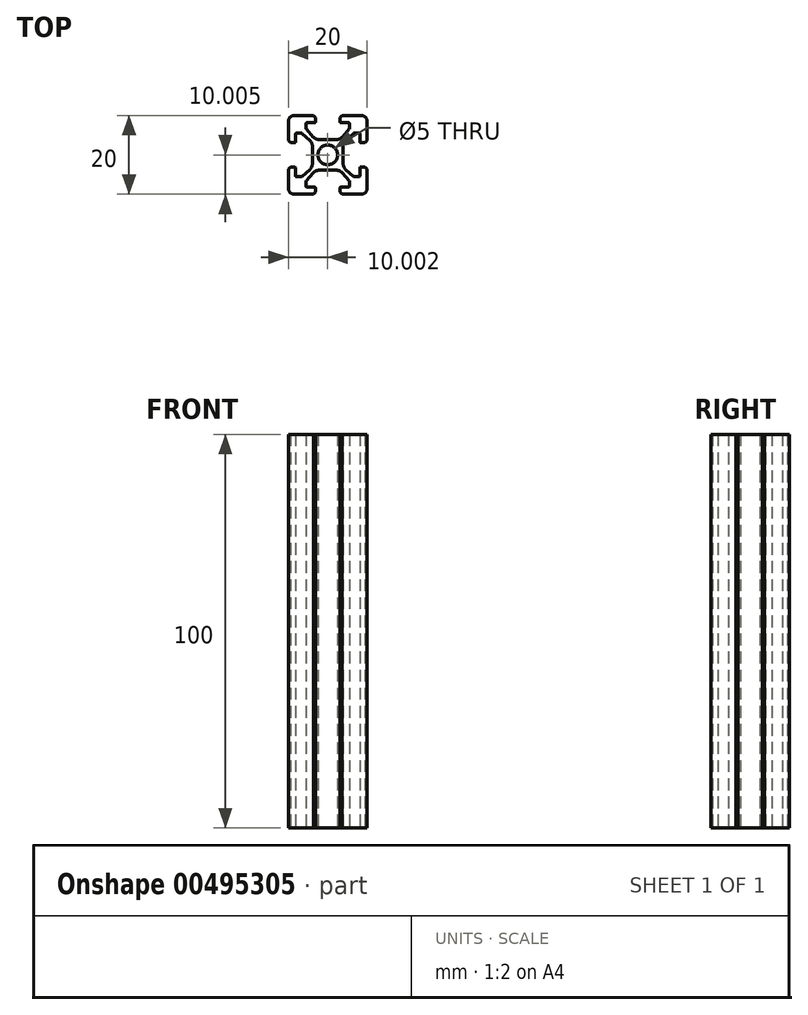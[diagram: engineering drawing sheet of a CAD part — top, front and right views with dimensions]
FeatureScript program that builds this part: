
annotation { "Feature Type Name" : "Feature", "Feature Type Description" : "" }
export const myFeature = defineFeature(function(context is Context, id is Id, definition is map)
    precondition{}
    {
        {
            var Q0;
            Q0=qCreatedBy(makeId("Top.planeOp"),FACE);
            var sketch = newSketch(context, id + "F0", { "sketchPlane" : qUnion([Q0])});
            skLineSegment(sketch, "E0", {"start": v(30.58, 14.76) * mm, "end": v(30.58, 13.66) * mm});
            skLineSegment(sketch, "E1", {"start": v(30.38, 13.46) * mm, "end": v(28.38, 13.46) * mm});
            skLineSegment(sketch, "E2", {"start": v(28.18, 13.26) * mm, "end": v(28.18, 11.94) * mm});
            skLineSegment(sketch, "E3", {"start": v(28.23, 11.8) * mm, "end": v(29.99, 9.84) * mm});
            skLineSegment(sketch, "E4", {"start": v(31.48, 9.16) * mm, "end": v(33.68, 9.16) * mm});
            skPoint(sketch, "E5.visualSharp", {"position": v(23.68, 15.26) * mm});
            skArc(sketch, "E5.filletArc", {"start": v(25.18, 15.26) * mm, "mid": v(24.6, 15.15) * mm, "end": v(24.1, 14.81) * mm});
            skPoint(sketch, "E6.visualSharp", {"position": v(30.58, 9.16) * mm});
            skArc(sketch, "E6.filletArc", {"start": v(29.99, 9.84) * mm, "mid": v(30.66, 9.34) * mm, "end": v(31.48, 9.16) * mm});
            skLineSegment(sketch, "E7", {"start": v(25.18, 15.26) * mm, "end": v(30.08, 15.26) * mm});
            skPoint(sketch, "E8.visualSharp", {"position": v(30.08, 14.76) * mm});
            skPoint(sketch, "E9.visualSharp", {"position": v(30.58, 13.46) * mm});
            skArc(sketch, "E9.filletArc", {"start": v(30.38, 13.46) * mm, "mid": v(30.52, 13.52) * mm, "end": v(30.58, 13.66) * mm});
            skPoint(sketch, "E10.visualSharp", {"position": v(28.18, 13.46) * mm});
            skArc(sketch, "E10.filletArc", {"start": v(28.38, 13.46) * mm, "mid": v(28.24, 13.4) * mm, "end": v(28.18, 13.26) * mm});
            skPoint(sketch, "E11.visualSharp", {"position": v(28.18, 11.86) * mm});
            skArc(sketch, "E11.filletArc", {"start": v(28.18, 11.94) * mm, "mid": v(28.2, 11.87) * mm, "end": v(28.23, 11.8) * mm});
            skLineSegment(sketch, "E12", {"start": v(30.08, 15.26) * mm, "end": v(30.58, 14.76) * mm});
            skLineSegment(sketch, "E13", {"start": v(24.12, 14.83) * mm, "end": v(24.12, 14.83) * mm});
            skArc(sketch, "E14.MirrorCS", {"start": v(25.48, 8.56) * mm, "mid": v(25.42, 8.42) * mm, "end": v(25.28, 8.36) * mm});
            skArc(sketch, "E15.MirrorCS", {"start": v(27, 10.76) * mm, "mid": v(27.08, 10.75) * mm, "end": v(27.14, 10.71) * mm});
            skArc(sketch, "E16.MirrorCS", {"start": v(25.48, 10.56) * mm, "mid": v(25.54, 10.7) * mm, "end": v(25.68, 10.76) * mm});
            skPoint(sketch, "E17.MirrorP", {"position": v(27.08, 10.76) * mm});
            skLineSegment(sketch, "E18.MirrorCS", {"start": v(23.68, 8.86) * mm, "end": v(24.18, 8.36) * mm});
            skLineSegment(sketch, "E19.MirrorCS", {"start": v(23.68, 13.76) * mm, "end": v(23.68, 8.86) * mm});
            skLineSegment(sketch, "E20.MirrorCS", {"start": v(25.68, 10.76) * mm, "end": v(27, 10.76) * mm});
            skLineSegment(sketch, "E21.MirrorCS", {"start": v(29.78, 7.47) * mm, "end": v(29.78, 5.26) * mm});
            skLineSegment(sketch, "E22.MirrorCS", {"start": v(27.14, 10.71) * mm, "end": v(29.11, 8.96) * mm});
            skLineSegment(sketch, "E23.MirrorCS", {"start": v(25.48, 8.56) * mm, "end": v(25.48, 10.56) * mm});
            skArc(sketch, "E24.MirrorCS", {"start": v(23.68, 13.76) * mm, "mid": v(23.8, 14.35) * mm, "end": v(24.13, 14.84) * mm});
            skPoint(sketch, "E25.MirrorP", {"position": v(29.78, 8.36) * mm});
            skPoint(sketch, "E26.MirrorP", {"position": v(25.48, 10.76) * mm});
            skPoint(sketch, "E27.MirrorP", {"position": v(24.18, 8.86) * mm});
            skPoint(sketch, "E28.MirrorP", {"position": v(25.48, 8.36) * mm});
            skLineSegment(sketch, "E29.MirrorCS", {"start": v(24.18, 8.36) * mm, "end": v(25.28, 8.36) * mm});
            skArc(sketch, "E30.MirrorCS", {"start": v(29.11, 8.96) * mm, "mid": v(29.6, 8.29) * mm, "end": v(29.78, 7.47) * mm});
            skArc(sketch, "E31.MirrorCS", {"start": v(39.18, 11.94) * mm, "mid": v(39.17, 11.87) * mm, "end": v(39.13, 11.8) * mm});
            skArc(sketch, "E32.MirrorCS", {"start": v(40.36, 10.76) * mm, "mid": v(40.29, 10.75) * mm, "end": v(40.23, 10.71) * mm});
            skArc(sketch, "E33.MirrorCS", {"start": v(41.88, 8.56) * mm, "mid": v(41.94, 8.42) * mm, "end": v(42.08, 8.36) * mm});
            skArc(sketch, "E34.MirrorCS", {"start": v(38.98, 13.46) * mm, "mid": v(39.12, 13.4) * mm, "end": v(39.18, 13.26) * mm});
            skArc(sketch, "E35.MirrorCS", {"start": v(36.98, 13.46) * mm, "mid": v(36.84, 13.52) * mm, "end": v(36.78, 13.66) * mm});
            skArc(sketch, "E36.MirrorCS", {"start": v(41.88, 10.56) * mm, "mid": v(41.82, 10.7) * mm, "end": v(41.68, 10.76) * mm});
            skArc(sketch, "E37.MirrorCS", {"start": v(42.18, 15.26) * mm, "mid": v(42.76, 15.15) * mm, "end": v(43.26, 14.81) * mm});
            skLineSegment(sketch, "E38.MirrorCS", {"start": v(37.28, 15.26) * mm, "end": v(36.78, 14.76) * mm});
            skArc(sketch, "E39.MirrorCS", {"start": v(43.68, 13.76) * mm, "mid": v(43.56, 14.35) * mm, "end": v(43.23, 14.84) * mm});
            skLineSegment(sketch, "E40.MirrorCS", {"start": v(43.18, 8.36) * mm, "end": v(42.08, 8.36) * mm});
            skLineSegment(sketch, "E41.MirrorCS", {"start": v(36.78, 14.76) * mm, "end": v(36.78, 13.66) * mm});
            skLineSegment(sketch, "E42.MirrorCS", {"start": v(43.68, 8.86) * mm, "end": v(43.18, 8.36) * mm});
            skLineSegment(sketch, "E43.MirrorCS", {"start": v(39.18, 13.26) * mm, "end": v(39.18, 11.94) * mm});
            skArc(sketch, "E44.MirrorCS", {"start": v(38.25, 8.96) * mm, "mid": v(37.76, 8.29) * mm, "end": v(37.58, 7.47) * mm});
            skLineSegment(sketch, "E45.MirrorCS", {"start": v(36.98, 13.46) * mm, "end": v(38.98, 13.46) * mm});
            skArc(sketch, "E46.MirrorCS", {"start": v(37.38, 9.84) * mm, "mid": v(36.7, 9.34) * mm, "end": v(35.88, 9.16) * mm});
            skLineSegment(sketch, "E47.MirrorCS", {"start": v(43.24, 14.83) * mm, "end": v(43.24, 14.83) * mm});
            skPoint(sketch, "E48.MirrorP", {"position": v(43.18, 8.86) * mm});
            skLineSegment(sketch, "E49.MirrorCS", {"start": v(39.13, 11.8) * mm, "end": v(37.38, 9.84) * mm});
            skLineSegment(sketch, "E50.MirrorCS", {"start": v(41.88, 8.56) * mm, "end": v(41.88, 10.56) * mm});
            skPoint(sketch, "E51.MirrorP", {"position": v(41.88, 8.36) * mm});
            skLineSegment(sketch, "E52.MirrorCS", {"start": v(43.68, 13.76) * mm, "end": v(43.68, 8.86) * mm});
            skLineSegment(sketch, "E53.MirrorCS", {"start": v(42.18, 15.26) * mm, "end": v(37.28, 15.26) * mm});
            skPoint(sketch, "E54.MirrorP", {"position": v(41.88, 10.76) * mm});
            skPoint(sketch, "E55.MirrorP", {"position": v(36.78, 13.46) * mm});
            skLineSegment(sketch, "E56.MirrorCS", {"start": v(35.88, 9.16) * mm, "end": v(33.68, 9.16) * mm});
            skPoint(sketch, "E57.MirrorP", {"position": v(37.58, 8.36) * mm});
            skLineSegment(sketch, "E58.MirrorCS", {"start": v(37.58, 7.47) * mm, "end": v(37.58, 5.26) * mm});
            skPoint(sketch, "E59.MirrorP", {"position": v(37.28, 14.76) * mm});
            skLineSegment(sketch, "E60.MirrorCS", {"start": v(41.68, 10.76) * mm, "end": v(40.36, 10.76) * mm});
            skLineSegment(sketch, "E61.MirrorCS", {"start": v(40.23, 10.71) * mm, "end": v(38.25, 8.96) * mm});
            skPoint(sketch, "E62.MirrorP", {"position": v(43.68, 15.26) * mm});
            skPoint(sketch, "E63.MirrorP", {"position": v(36.78, 9.16) * mm});
            skPoint(sketch, "E64.MirrorP", {"position": v(39.18, 11.86) * mm});
            skPoint(sketch, "E65.MirrorP", {"position": v(40.28, 10.76) * mm});
            skPoint(sketch, "E66.MirrorP", {"position": v(39.18, 13.46) * mm});
            skArc(sketch, "E67.MirrorCS", {"start": v(40.36, -0.24) * mm, "mid": v(40.29, -0.22) * mm, "end": v(40.23, -0.18) * mm});
            skArc(sketch, "E68.MirrorCS", {"start": v(28.18, -1.41) * mm, "mid": v(28.2, -1.34) * mm, "end": v(28.23, -1.28) * mm});
            skLineSegment(sketch, "E69.MirrorCS", {"start": v(41.68, -0.24) * mm, "end": v(40.36, -0.24) * mm});
            skArc(sketch, "E70.MirrorCS", {"start": v(27, -0.24) * mm, "mid": v(27.08, -0.22) * mm, "end": v(27.14, -0.18) * mm});
            skArc(sketch, "E71.MirrorCS", {"start": v(41.88, -0.04) * mm, "mid": v(41.82, -0.18) * mm, "end": v(41.68, -0.24) * mm});
            skArc(sketch, "E72.MirrorCS", {"start": v(28.38, -2.94) * mm, "mid": v(28.24, -2.88) * mm, "end": v(28.18, -2.74) * mm});
            skLineSegment(sketch, "E73.MirrorCS", {"start": v(28.18, -2.74) * mm, "end": v(28.18, -1.41) * mm});
            skLineSegment(sketch, "E74.MirrorCS", {"start": v(25.68, -0.24) * mm, "end": v(27, -0.24) * mm});
            skArc(sketch, "E75.MirrorCS", {"start": v(25.48, -0.04) * mm, "mid": v(25.54, -0.18) * mm, "end": v(25.68, -0.24) * mm});
            skArc(sketch, "E76.MirrorCS", {"start": v(38.98, -2.94) * mm, "mid": v(39.12, -2.88) * mm, "end": v(39.18, -2.74) * mm});
            skLineSegment(sketch, "E77.MirrorCS", {"start": v(30.58, -4.24) * mm, "end": v(30.58, -3.14) * mm});
            skArc(sketch, "E78.MirrorCS", {"start": v(41.88, 1.96) * mm, "mid": v(41.94, 2.1) * mm, "end": v(42.08, 2.16) * mm});
            skArc(sketch, "E79.MirrorCS", {"start": v(39.18, -1.41) * mm, "mid": v(39.17, -1.34) * mm, "end": v(39.13, -1.28) * mm});
            skLineSegment(sketch, "E80.MirrorCS", {"start": v(39.18, -2.74) * mm, "end": v(39.18, -1.41) * mm});
            skArc(sketch, "E81.MirrorCS", {"start": v(36.98, -2.94) * mm, "mid": v(36.84, -3) * mm, "end": v(36.78, -3.14) * mm});
            skLineSegment(sketch, "E82.MirrorCS", {"start": v(30.08, -4.74) * mm, "end": v(30.58, -4.24) * mm});
            skArc(sketch, "E83.MirrorCS", {"start": v(30.38, -2.94) * mm, "mid": v(30.52, -3) * mm, "end": v(30.58, -3.14) * mm});
            skArc(sketch, "E84.MirrorCS", {"start": v(25.48, 1.96) * mm, "mid": v(25.42, 2.1) * mm, "end": v(25.28, 2.16) * mm});
            skLineSegment(sketch, "E85.MirrorCS", {"start": v(23.68, 1.66) * mm, "end": v(24.18, 2.16) * mm});
            skArc(sketch, "E86.MirrorCS", {"start": v(23.68, -3.24) * mm, "mid": v(23.8, -3.82) * mm, "end": v(24.13, -4.3) * mm});
            skLineSegment(sketch, "E87.MirrorCS", {"start": v(37.28, -4.74) * mm, "end": v(36.78, -4.24) * mm});
            skArc(sketch, "E88.MirrorCS", {"start": v(43.68, -3.24) * mm, "mid": v(43.56, -3.82) * mm, "end": v(43.23, -4.3) * mm});
            skArc(sketch, "E89.MirrorCS", {"start": v(29.99, 0.7) * mm, "mid": v(30.66, 1.19) * mm, "end": v(31.48, 1.36) * mm});
            skArc(sketch, "E90.MirrorCS", {"start": v(42.18, -4.74) * mm, "mid": v(42.76, -4.62) * mm, "end": v(43.26, -4.28) * mm});
            skArc(sketch, "E91.MirrorCS", {"start": v(37.38, 0.7) * mm, "mid": v(36.7, 1.19) * mm, "end": v(35.88, 1.36) * mm});
            skLineSegment(sketch, "E92.MirrorCS", {"start": v(36.78, -4.24) * mm, "end": v(36.78, -3.14) * mm});
            skLineSegment(sketch, "E93.MirrorCS", {"start": v(43.68, 1.66) * mm, "end": v(43.18, 2.16) * mm});
            skArc(sketch, "E94.MirrorCS", {"start": v(38.25, 1.57) * mm, "mid": v(37.76, 2.24) * mm, "end": v(37.58, 3.06) * mm});
            skArc(sketch, "E95.MirrorCS", {"start": v(29.11, 1.57) * mm, "mid": v(29.6, 2.24) * mm, "end": v(29.78, 3.06) * mm});
            skLineSegment(sketch, "E96.MirrorCS", {"start": v(24.18, 2.16) * mm, "end": v(25.28, 2.16) * mm});
            skArc(sketch, "E97.MirrorCS", {"start": v(25.18, -4.74) * mm, "mid": v(24.6, -4.62) * mm, "end": v(24.1, -4.28) * mm});
            skLineSegment(sketch, "E98.MirrorCS", {"start": v(43.18, 2.16) * mm, "end": v(42.08, 2.16) * mm});
            skLineSegment(sketch, "E99.MirrorCS", {"start": v(43.24, -4.3) * mm, "end": v(43.24, -4.3) * mm});
            skPoint(sketch, "E100.MirrorP", {"position": v(28.18, -1.34) * mm});
            skLineSegment(sketch, "E101.MirrorCS", {"start": v(24.12, -4.3) * mm, "end": v(24.12, -4.3) * mm});
            skLineSegment(sketch, "E102.MirrorCS", {"start": v(30.38, -2.94) * mm, "end": v(28.38, -2.94) * mm});
            skPoint(sketch, "E103.MirrorP", {"position": v(23.68, -4.74) * mm});
            skPoint(sketch, "E104.MirrorP", {"position": v(28.18, -2.94) * mm});
            skPoint(sketch, "E105.MirrorP", {"position": v(37.28, -4.24) * mm});
            skPoint(sketch, "E106.MirrorP", {"position": v(25.48, 2.16) * mm});
            skPoint(sketch, "E107.MirrorP", {"position": v(37.58, 2.16) * mm});
            skPoint(sketch, "E108.MirrorP", {"position": v(30.08, -4.24) * mm});
            skPoint(sketch, "E109.MirrorP", {"position": v(41.88, -0.24) * mm});
            skPoint(sketch, "E110.MirrorP", {"position": v(30.58, 1.36) * mm});
            skPoint(sketch, "E111.MirrorP", {"position": v(29.78, 2.16) * mm});
            skPoint(sketch, "E112.MirrorP", {"position": v(41.88, 2.16) * mm});
            skPoint(sketch, "E113.MirrorP", {"position": v(43.68, -4.74) * mm});
            skLineSegment(sketch, "E114.MirrorCS", {"start": v(39.13, -1.28) * mm, "end": v(37.38, 0.7) * mm});
            skLineSegment(sketch, "E115.MirrorCS", {"start": v(36.98, -2.94) * mm, "end": v(38.98, -2.94) * mm});
            skLineSegment(sketch, "E116.MirrorCS", {"start": v(28.23, -1.28) * mm, "end": v(29.99, 0.7) * mm});
            skPoint(sketch, "E117.MirrorP", {"position": v(24.18, 1.66) * mm});
            skPoint(sketch, "E118.MirrorP", {"position": v(43.18, 1.66) * mm});
            skPoint(sketch, "E119.MirrorP", {"position": v(36.78, 1.36) * mm});
            skLineSegment(sketch, "E120.MirrorCS", {"start": v(43.68, -3.24) * mm, "end": v(43.68, 1.66) * mm});
            skPoint(sketch, "E121.MirrorP", {"position": v(30.58, -2.94) * mm});
            skLineSegment(sketch, "E122.MirrorCS", {"start": v(31.48, 1.36) * mm, "end": v(33.68, 1.36) * mm});
            skPoint(sketch, "E123.MirrorP", {"position": v(40.28, -0.24) * mm});
            skLineSegment(sketch, "E124.MirrorCS", {"start": v(25.48, 1.96) * mm, "end": v(25.48, -0.04) * mm});
            skPoint(sketch, "E125.MirrorP", {"position": v(27.08, -0.24) * mm});
            skLineSegment(sketch, "E126.MirrorCS", {"start": v(27.14, -0.18) * mm, "end": v(29.11, 1.57) * mm});
            skLineSegment(sketch, "E127.MirrorCS", {"start": v(35.88, 1.36) * mm, "end": v(33.68, 1.36) * mm});
            skLineSegment(sketch, "E128.MirrorCS", {"start": v(29.78, 3.06) * mm, "end": v(29.78, 5.26) * mm});
            skLineSegment(sketch, "E129.MirrorCS", {"start": v(37.58, 3.06) * mm, "end": v(37.58, 5.26) * mm});
            skLineSegment(sketch, "E130.MirrorCS", {"start": v(40.23, -0.18) * mm, "end": v(38.25, 1.57) * mm});
            skPoint(sketch, "E131.MirrorP", {"position": v(36.78, -2.94) * mm});
            skPoint(sketch, "E132.MirrorP", {"position": v(39.18, -2.94) * mm});
            skLineSegment(sketch, "E133.MirrorCS", {"start": v(42.18, -4.74) * mm, "end": v(37.28, -4.74) * mm});
            skPoint(sketch, "E134.MirrorP", {"position": v(39.18, -1.34) * mm});
            skLineSegment(sketch, "E135.MirrorCS", {"start": v(25.18, -4.74) * mm, "end": v(30.08, -4.74) * mm});
            skLineSegment(sketch, "E136.MirrorCS", {"start": v(41.88, 1.96) * mm, "end": v(41.88, -0.04) * mm});
            skLineSegment(sketch, "E137.MirrorCS", {"start": v(23.68, -3.24) * mm, "end": v(23.68, 1.66) * mm});
            skPoint(sketch, "E138.MirrorP", {"position": v(25.48, -0.24) * mm});
            skCircle(sketch, "E139", {"center": v(33.68, 5.26) * mm, "radius": 2.5 * mm});
            skSolve(sketch);
        }
        {
            var Q0;
            Q0=makeQuery(id+"F0.imprint","IMPRINT",FACE,{"disambiguationData":[TD([[makeQuery(id+"F0.imprint","IMPRINT",EDGE,{"derivedFrom":sQuery(id+"F0.wireOp",EDGE,"E0")}),-1.0]])]});
            extrude(context, id + "F1", {"entities" : qUnion([Q0]), "depth" : 100 * mm});
        }
    });
